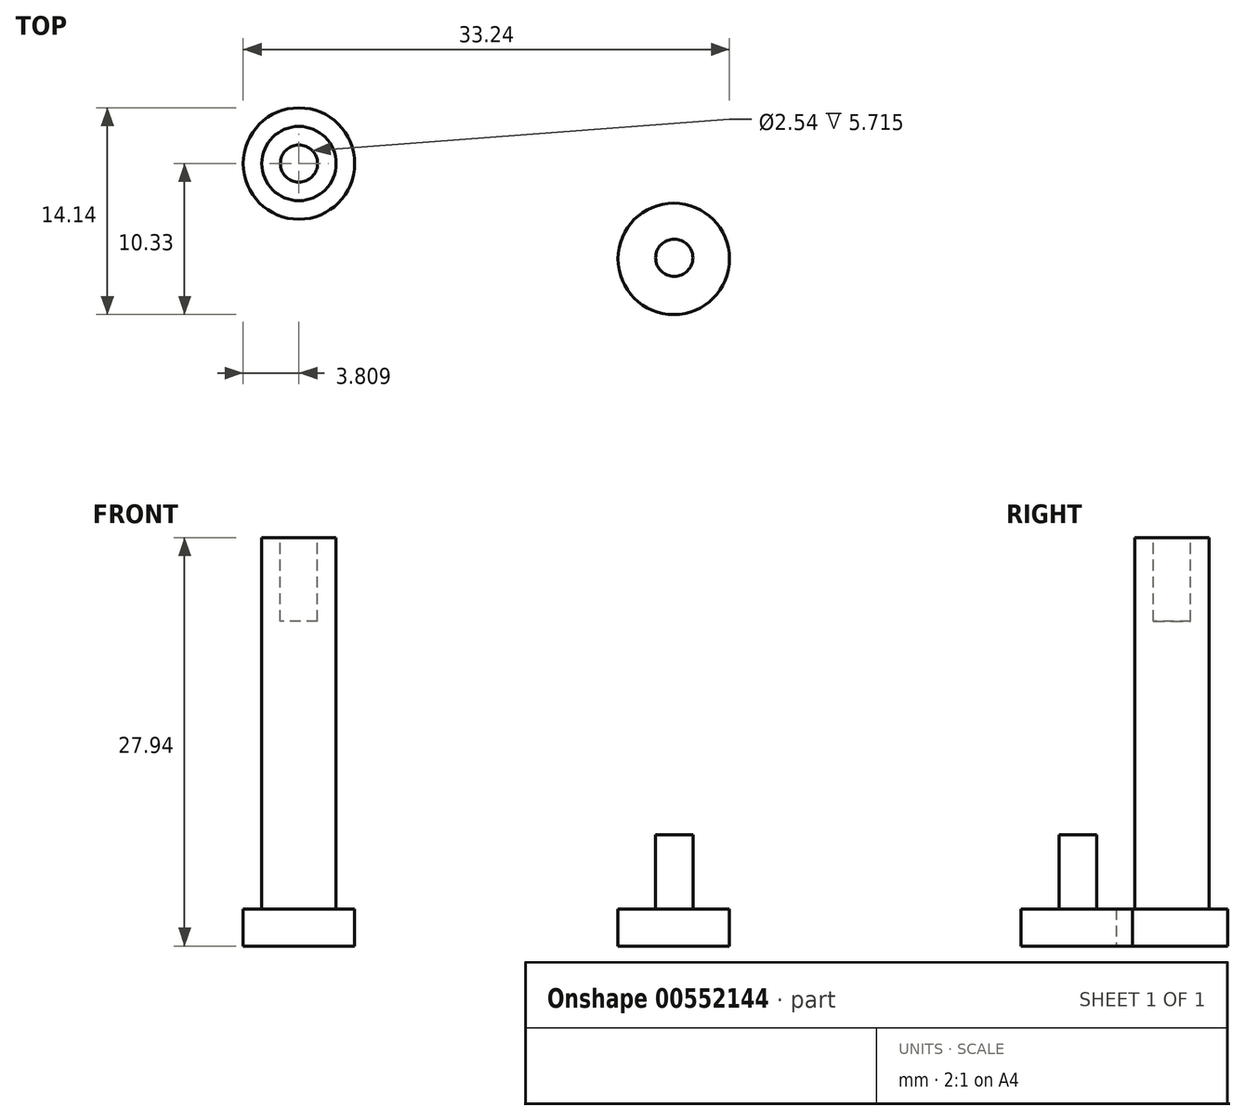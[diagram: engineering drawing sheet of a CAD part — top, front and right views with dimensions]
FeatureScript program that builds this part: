
annotation { "Feature Type Name" : "Feature", "Feature Type Description" : "" }
export const myFeature = defineFeature(function(context is Context, id is Id, definition is map)
    precondition{}
    {
        {
            var Q0;
            Q0=qCreatedBy(makeId("Top.planeOp"),FACE);
            var sketch = newSketch(context, id + "F0", { "sketchPlane" : qUnion([Q0])});
            skCircle(sketch, "E0", {"center": v(-12.8, 7.95) * mm, "radius": 3.81 * mm});
            skCircle(sketch, "E1", {"center": v(12.83, 1.43) * mm, "radius": 3.81 * mm});
            skSolve(sketch);
        }
        {
            var Q0;
            Q0=makeQuery(id+"F0.imprint","IMPRINT",FACE,{"disambiguationData":[TD([[makeQuery(id+"F0.imprint","IMPRINT",EDGE,{"derivedFrom":sQuery(id+"F0.wireOp",EDGE,"E1")}),1.0]])]});
            var Q1;
            Q1=makeQuery(id+"F0.imprint","IMPRINT",FACE,{"disambiguationData":[TD([[makeQuery(id+"F0.imprint","IMPRINT",EDGE,{"derivedFrom":sQuery(id+"F0.wireOp",EDGE,"E0")}),1.0]])]});
            extrude(context, id + "F1", {"entities" : qUnion([Q0, Q1]), "depth" : 2.54 * mm, "offsetDistance" : 25.4 * mm});
        }
        {
            var Q0;
            Q0=makeQuery(id+"F1.opExtrude","CAP_FACE",FACE,{"disambiguationData":[OSD([sQuery(id+"F0.wireOp",EDGE,"E0")])],"isStart":false});
            var sketch = newSketch(context, id + "F2", { "sketchPlane" : qUnion([Q0])});
            skCircle(sketch, "E2", {"center": v(12.87, 1.5) * mm, "radius": 1.27 * mm});
            skSolve(sketch);
        }
        {
            var Q0;
            Q0 = qSketchRegion(id + "F2", true);
            extrude(context, id + "F3", {"entities" : qUnion([Q0]), "depth" : 5.08 * mm, "offsetDistance" : 25.4 * mm});
        }
        {
            var Q0;
            Q0=makeQuery(id+"F1.opExtrude","CAP_FACE",FACE,{"disambiguationData":[OSD([sQuery(id+"F0.wireOp",EDGE,"E0")])],"isStart":false});
            var sketch = newSketch(context, id + "F4", { "sketchPlane" : qUnion([Q0])});
            skCircle(sketch, "E3", {"center": v(-12.8, 7.95) * mm, "radius": 2.54 * mm});
            skSolve(sketch);
        }
        {
            var Q0;
            Q0=makeQuery(id+"F4.imprint","IMPRINT",FACE,{"disambiguationData":[TD([[makeQuery(id+"F4.imprint","IMPRINT",EDGE,{"derivedFrom":sQuery(id+"F4.wireOp",EDGE,"E3")}),1.0]])]});
            extrude(context, id + "F5", {"entities" : qUnion([Q0]), "operationType" : NewBodyOperationType.ADD, "depth" : 25.4 * mm, "offsetDistance" : 25.4 * mm});
        }
        {
            var Q0;
            Q0=makeQuery(id+"F5.opExtrude","CAP_FACE",FACE,{"disambiguationData":[OSD([sQuery(id+"F4.wireOp",EDGE,"E3")])],"isStart":false});
            var sketch = newSketch(context, id + "F6", { "sketchPlane" : qUnion([Q0])});
            skCircle(sketch, "E4", {"center": v(-12.8, 7.95) * mm, "radius": 1.27 * mm});
            skSolve(sketch);
        }
        {
            var Q0;
            Q0 = qSketchRegion(id + "F6", true);
            extrude(context, id + "F7", {"entities" : qUnion([Q0]), "operationType" : NewBodyOperationType.REMOVE, "oppositeDirection" : true, "depth" : 5.7 * mm, "offsetDistance" : 25.4 * mm});
        }
    });
